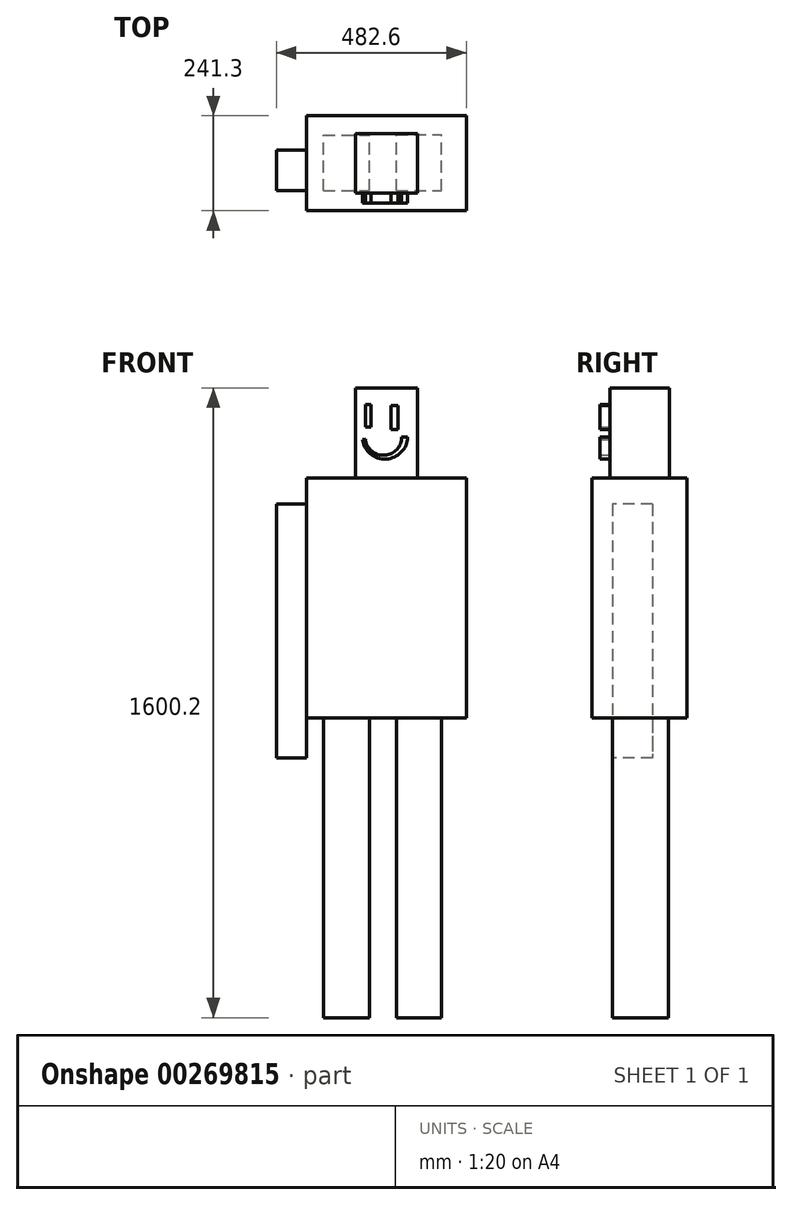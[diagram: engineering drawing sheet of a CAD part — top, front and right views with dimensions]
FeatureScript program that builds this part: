
annotation { "Feature Type Name" : "Feature", "Feature Type Description" : "" }
export const myFeature = defineFeature(function(context is Context, id is Id, definition is map)
    precondition{}
    {
        {
            var Q0;
            Q0=qCreatedBy(makeId("Front.planeOp"),FACE);
            var sketch = newSketch(context, id + "F0", { "sketchPlane" : qUnion([Q0])});
            skLineSegment(sketch, "E0.bottom", {"start": v(-204.16, 387.6) * mm, "end": v(202.24, 387.6) * mm});
            skLineSegment(sketch, "E0.top", {"start": v(-204.16, -222) * mm, "end": v(202.24, -222) * mm});
            skLineSegment(sketch, "E0.left", {"start": v(-204.16, 387.6) * mm, "end": v(-204.16, -222) * mm});
            skLineSegment(sketch, "E0.right", {"start": v(202.24, 387.6) * mm, "end": v(202.24, -222) * mm});
            skSolve(sketch);
        }
        {
            var Q0;
            Q0=makeQuery(id+"F0.imprint","IMPRINT",FACE,{"disambiguationData":[TD([[makeQuery(id+"F0.imprint","IMPRINT",EDGE,{"derivedFrom":sQuery(id+"F0.wireOp",EDGE,"E0.bottom")}),-1.0]])]});
            extrude(context, id + "F1", {"entities" : qUnion([Q0]), "depth" : 241.3 * mm});
        }
        {
            var Q0;
            Q0=makeQuery(id+"F1.opExtrude","SWEPT_FACE",FACE,{"disambiguationData":[OSD([sQuery(id+"F0.wireOp",EDGE,"E0.bottom")])]});
            var sketch = newSketch(context, id + "F2", { "sketchPlane" : qUnion([Q0])});
            skLineSegment(sketch, "E1.bottom", {"start": v(78.88, -196.62) * mm, "end": v(-78.88, -196.62) * mm});
            skLineSegment(sketch, "E1.top", {"start": v(78.88, -44.68) * mm, "end": v(-78.88, -44.68) * mm});
            skLineSegment(sketch, "E1.left", {"start": v(78.88, -196.62) * mm, "end": v(78.88, -44.68) * mm});
            skLineSegment(sketch, "E1.right", {"start": v(-78.88, -196.62) * mm, "end": v(-78.88, -44.68) * mm});
            skPoint(sketch, "E1.middle", {"position": v(0, -120.65) * mm});
            skPoint(sketch, "E1.middle.positionSnap0", {"position": v(202.24, -120.65) * mm});
            skPoint(sketch, "E1.centerSnap0", {"position": v(202.24, -120.65) * mm});
            skSolve(sketch);
        }
        {
            var Q0;
            Q0=makeQuery(id+"F2.imprint","IMPRINT",FACE,{"disambiguationData":[TD([[makeQuery(id+"F2.imprint","IMPRINT",EDGE,{"derivedFrom":sQuery(id+"F2.wireOp",EDGE,"E1.bottom")}),-1.0]])]});
            extrude(context, id + "F3", {"entities" : qUnion([Q0]), "operationType" : NewBodyOperationType.ADD, "depth" : 228.6 * mm});
        }
        {
            var Q0;
            Q0=makeQuery(id+"F1.opExtrude","SWEPT_FACE",FACE,{"disambiguationData":[OSD([sQuery(id+"F0.wireOp",EDGE,"E0.left")])]});
            var sketch = newSketch(context, id + "F4", { "sketchPlane" : qUnion([Q0])});
            skLineSegment(sketch, "E2.bottom", {"start": v(87.74, 320.95) * mm, "end": v(190.21, 320.95) * mm});
            skLineSegment(sketch, "E2.top", {"start": v(87.74, -323.4) * mm, "end": v(190.21, -323.4) * mm});
            skLineSegment(sketch, "E2.left", {"start": v(87.74, 320.95) * mm, "end": v(87.74, -323.4) * mm});
            skLineSegment(sketch, "E2.right", {"start": v(190.21, 320.95) * mm, "end": v(190.21, -323.4) * mm});
            skSolve(sketch);
        }
        {
            var Q0;
            {var subQ0=sQuery(id+"F4.wireOp",EDGE,"E2.bottom");Q0=makeQuery(id+"F4.imprint","IMPRINT",FACE,{"disambiguationData":[TD([[makeQuery(id+"F4.imprint","IMPRINT",EDGE,{"derivedFrom":subQ0}),-1.0]])]});}
            var Q1;
            {var subQ0=sQuery(id+"F4.wireOp",EDGE,"E2.top");Q1=makeQuery(id+"F4.imprint","IMPRINT",FACE,{"disambiguationData":[TD([[makeQuery(id+"F4.imprint","IMPRINT",EDGE,{"derivedFrom":subQ0}),1.0]])]});}
            extrude(context, id + "F5", {"entities" : qUnion([Q0, Q1]), "operationType" : NewBodyOperationType.ADD, "depth" : 76.2 * mm});
        }
        {
            var Q0;
            Q0=makeQuery(id+"F1.opExtrude","SWEPT_FACE",FACE,{"disambiguationData":[OSD([sQuery(id+"F0.wireOp",EDGE,"E0.top")])]});
            var sketch = newSketch(context, id + "F6", { "sketchPlane" : qUnion([Q0])});
            skLineSegment(sketch, "E3.bottom", {"start": v(-160.52, 190.21) * mm, "end": v(-43.31, 190.21) * mm});
            skLineSegment(sketch, "E3.top", {"start": v(-160.52, 48.6) * mm, "end": v(-43.31, 48.6) * mm});
            skLineSegment(sketch, "E3.left", {"start": v(-160.52, 190.21) * mm, "end": v(-160.52, 48.6) * mm});
            skLineSegment(sketch, "E3.right", {"start": v(-43.31, 190.21) * mm, "end": v(-43.31, 48.6) * mm});
            skLineSegment(sketch, "E4.bottom", {"start": v(24.44, 190.21) * mm, "end": v(139.5, 190.21) * mm});
            skLineSegment(sketch, "E4.top", {"start": v(24.44, 48.1) * mm, "end": v(139.5, 48.1) * mm});
            skLineSegment(sketch, "E4.left", {"start": v(24.44, 190.21) * mm, "end": v(24.44, 48.1) * mm});
            skLineSegment(sketch, "E4.right", {"start": v(139.5, 190.21) * mm, "end": v(139.5, 48.1) * mm});
            skSolve(sketch);
        }
        {
            var Q0;
            Q0=makeQuery(id+"F6.imprint","IMPRINT",FACE,{"disambiguationData":[TD([[makeQuery(id+"F6.imprint","IMPRINT",EDGE,{"derivedFrom":sQuery(id+"F6.wireOp",EDGE,"E3.bottom")}),-1.0]])]});
            var Q1;
            Q1=makeQuery(id+"F6.imprint","IMPRINT",FACE,{"disambiguationData":[TD([[makeQuery(id+"F6.imprint","IMPRINT",EDGE,{"derivedFrom":sQuery(id+"F6.wireOp",EDGE,"E4.bottom")}),-1.0]])]});
            extrude(context, id + "F7", {"entities" : qUnion([Q0, Q1]), "operationType" : NewBodyOperationType.ADD, "depth" : 762 * mm});
        }
        {
            var Q0;
            Q0=makeQuery(id+"F3.opExtrude","SWEPT_FACE",FACE,{"disambiguationData":[OSD([sQuery(id+"F2.wireOp",EDGE,"E1.bottom")])]});
            var sketch = newSketch(context, id + "F8", { "sketchPlane" : qUnion([Q0])});
            skArc(sketch, "E5", {"start": v(-61.68, 484.86) * mm, "mid": v(-1.26, 435.53) * mm, "end": v(53.6, 490.97) * mm});
            skLineSegment(sketch, "E6.bottom", {"start": v(-54.1, 574.49) * mm, "end": v(-39.44, 574.49) * mm});
            skLineSegment(sketch, "E6.top", {"start": v(-54.1, 517.06) * mm, "end": v(-39.44, 517.06) * mm});
            skLineSegment(sketch, "E6.left", {"start": v(-54.1, 574.49) * mm, "end": v(-54.1, 517.06) * mm});
            skLineSegment(sketch, "E6.right", {"start": v(-39.44, 574.49) * mm, "end": v(-39.44, 517.06) * mm});
            skLineSegment(sketch, "E7.bottom", {"start": v(10.9, 571.97) * mm, "end": v(29.16, 571.97) * mm});
            skLineSegment(sketch, "E7.top", {"start": v(10.9, 510.43) * mm, "end": v(29.16, 510.43) * mm});
            skLineSegment(sketch, "E7.left", {"start": v(10.9, 571.97) * mm, "end": v(10.9, 510.43) * mm});
            skLineSegment(sketch, "E7.right", {"start": v(29.16, 571.97) * mm, "end": v(29.16, 510.43) * mm});
            skArc(sketch, "E8", {"start": v(-54.1, 485.68) * mm, "mid": v(-5.12, 445.1) * mm, "end": v(38.31, 491.56) * mm});
            skLineSegment(sketch, "E9", {"start": v(-61.68, 484.86) * mm, "end": v(-54.1, 485.68) * mm});
            skLineSegment(sketch, "E10", {"start": v(38.31, 491.56) * mm, "end": v(53.6, 490.97) * mm});
            skSolve(sketch);
        }
        {
            var Q0;
            Q0=makeQuery(id+"F8.imprint","IMPRINT",FACE,{"disambiguationData":[TD([[makeQuery(id+"F8.imprint","IMPRINT",EDGE,{"derivedFrom":sQuery(id+"F8.wireOp",EDGE,"E6.bottom")}),-1.0]])]});
            var Q1;
            Q1=makeQuery(id+"F8.imprint","IMPRINT",FACE,{"disambiguationData":[TD([[makeQuery(id+"F8.imprint","IMPRINT",EDGE,{"derivedFrom":sQuery(id+"F8.wireOp",EDGE,"E7.bottom")}),-1.0]])]});
            var Q2;
            Q2=makeQuery(id+"F8.imprint","IMPRINT",FACE,{"disambiguationData":[TD([[makeQuery(id+"F8.imprint","IMPRINT",EDGE,{"derivedFrom":sQuery(id+"F8.wireOp",EDGE,"E5")}),1.0]])]});
            extrude(context, id + "F9", {"entities" : qUnion([Q0, Q1, Q2]), "operationType" : NewBodyOperationType.ADD, "depth" : 25.4 * mm});
        }
    });
